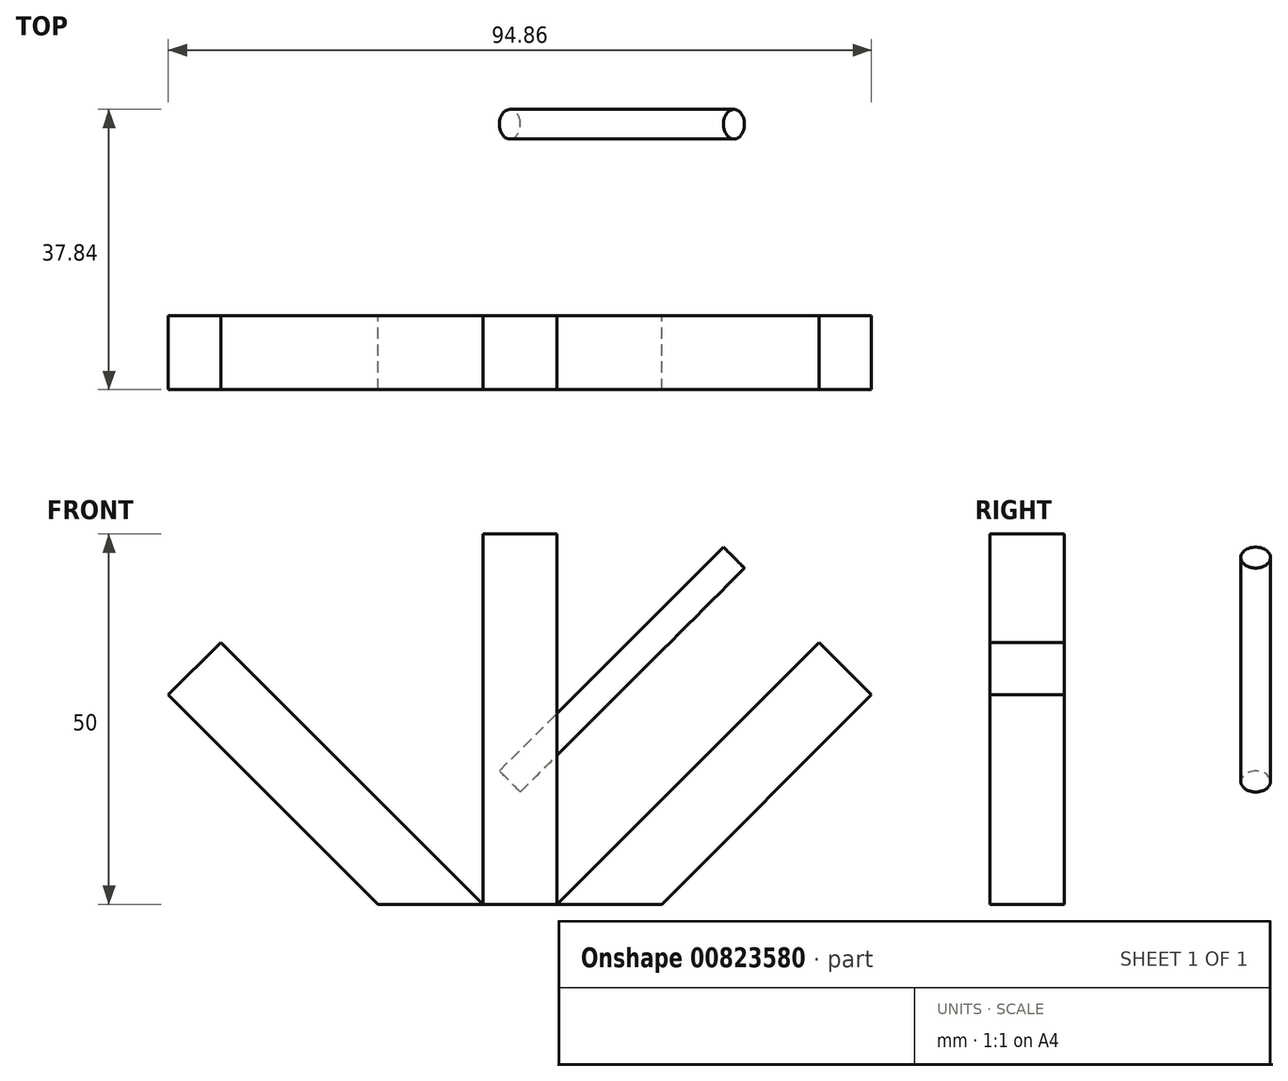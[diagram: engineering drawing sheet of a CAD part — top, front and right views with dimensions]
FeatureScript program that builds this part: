
annotation { "Feature Type Name" : "Feature", "Feature Type Description" : "" }
export const myFeature = defineFeature(function(context is Context, id is Id, definition is map)
    precondition{}
    {
        {
            var Q0;
            Q0=qCreatedBy(makeId("Front.planeOp"),FACE);
            var sketch = newSketch(context, id + "F0", { "sketchPlane" : qUnion([Q0])});
            skLineSegment(sketch, "E0.bottom", {"start": v(5.01, -25) * mm, "end": v(-4.99, -25) * mm});
            skLineSegment(sketch, "E0.left", {"start": v(5.01, -25) * mm, "end": v(5.01, 25) * mm});
            skLineSegment(sketch, "E0.right", {"start": v(-4.99, -25) * mm, "end": v(-4.99, 25) * mm});
            skPoint(sketch, "E0.middle", {"position": v(0.01, 0) * mm});
            skPoint(sketch, "E1.middle", {"position": v(0, -26.34) * mm});
            skLineSegment(sketch, "E2", {"start": v(5.01, -25) * mm, "end": v(40.37, 10.36) * mm});
            skLineSegment(sketch, "E3", {"start": v(19.15, -25) * mm, "end": v(5.01, -25) * mm});
            skLineSegment(sketch, "E4", {"start": v(0.01, -25) * mm, "end": v(-19.13, -25) * mm});
            skLineSegment(sketch, "E5", {"start": v(-19.13, -25) * mm, "end": v(19.15, -25) * mm});
            skLineSegment(sketch, "E6", {"start": v(40.37, 10.36) * mm, "end": v(47.44, 3.28) * mm});
            skLineSegment(sketch, "E7", {"start": v(47.44, 3.28) * mm, "end": v(19.15, -25) * mm});
            skLineSegment(sketch, "E8", {"start": v(-4.99, -25) * mm, "end": v(-40.35, 10.36) * mm});
            skLineSegment(sketch, "E9", {"start": v(-40.35, 10.36) * mm, "end": v(-47.42, 3.28) * mm});
            skLineSegment(sketch, "E10", {"start": v(-47.42, 3.28) * mm, "end": v(-19.13, -25) * mm});
            skPoint(sketch, "E11.orphan", {"position": v(-19.13, -25) * mm});
            skLineSegment(sketch, "E12", {"start": v(5.01, 25) * mm, "end": v(-4.99, 25) * mm});
            skSolve(sketch);
        }
        {
            var Q0;
            {var subQ0=sQuery(id+"F0.wireOp",EDGE,"E2");Q0=makeQuery(id+"F0.imprint","IMPRINT",FACE,{"disambiguationData":[TD([[makeQuery(id+"F0.imprint","IMPRINT",EDGE,{"derivedFrom":subQ0}),-1.0]])]});}
            var Q1;
            {var subQ0=sQuery(id+"F0.wireOp",EDGE,"E0.left");Q1=makeQuery(id+"F0.imprint","IMPRINT",FACE,{"disambiguationData":[TD([[makeQuery(id+"F0.imprint","IMPRINT",EDGE,{"derivedFrom":subQ0}),1.0]])]});}
            var Q2;
            {var subQ0=sQuery(id+"F0.wireOp",EDGE,"E8");Q2=makeQuery(id+"F0.imprint","IMPRINT",FACE,{"disambiguationData":[TD([[makeQuery(id+"F0.imprint","IMPRINT",EDGE,{"derivedFrom":subQ0}),1.0]])]});}
            extrude(context, id + "F1", {"entities" : qUnion([Q0, Q1, Q2]), "depth" : 10 * mm, "offsetDistance" : 25 * mm});
        }
        {
            var Q0;
            Q0=makeQuery(id+"F1.opExtrude","SWEPT_FACE",FACE,{"disambiguationData":[OSD([sQuery(id+"F0.wireOp",EDGE,"E9")])]});
            var sketch = newSketch(context, id + "F2", { "sketchPlane" : qUnion([Q0])});
            skCircle(sketch, "E13", {"center": v(5, -26.06) * mm, "radius": 2 * mm});
            skSolve(sketch);
        }
        {
            var Q0;
            Q0=sQuery(id+"F2.wireOp",EDGE,"E13");
            extrude(context, id + "F3", {"bodyType" : ToolBodyType.SURFACE, "surfaceEntities" : qUnion([Q0]), "oppositeDirection" : true, "depth" : 39.2 * mm, "offsetDistance" : 25 * mm});
        }
        {
            var Q0;
            Q0=makeQuery(id+"F1.opExtrude","SWEPT_FACE",FACE,{"disambiguationData":[OSD([sQuery(id+"F0.wireOp",EDGE,"E6")])]});
            var sketch = newSketch(context, id + "F4", { "sketchPlane" : qUnion([Q0])});
            skCircle(sketch, "E14", {"center": v(25.84, -5) * mm, "radius": 2 * mm});
            skPoint(sketch, "E14.centerSnap0", {"position": v(31.22, -5) * mm});
            skSolve(sketch);
        }
        {
            var Q0;
            Q0=sQuery(id+"F4.wireOp",EDGE,"E14");
            extrude(context, id + "F5", {"bodyType" : ToolBodyType.SURFACE, "surfaceEntities" : qUnion([Q0]), "oppositeDirection" : true, "depth" : 25 * mm, "offsetDistance" : 25 * mm});
        }
        {
            var Q0;
            Q0 = qSketchRegion(id + "F4", true);
            extrude(context, id + "F6", {"entities" : qUnion([Q0]), "operationType" : NewBodyOperationType.ADD, "oppositeDirection" : true, "depth" : 42.76 * mm, "offsetDistance" : 25 * mm});
        }
        {
            var Q0;
            Q0=makeQuery(id+"F1.opExtrude","SWEPT_FACE",FACE,{"disambiguationData":[OSD([sQuery(id+"F0.wireOp",EDGE,"E12")])]});
            var sketch = newSketch(context, id + "F7", { "sketchPlane" : qUnion([Q0])});
            skCircle(sketch, "E15", {"center": v(0, -5) * mm, "radius": 2 * mm});
            skSolve(sketch);
        }
        {
            var Q0;
            Q0=sQuery(id+"F7.wireOp",EDGE,"E15");
            extrude(context, id + "F8", {"bodyType" : ToolBodyType.SURFACE, "surfaceEntities" : qUnion([Q0]), "oppositeDirection" : true, "depth" : 48 * mm, "offsetDistance" : 25 * mm});
        }
    });
